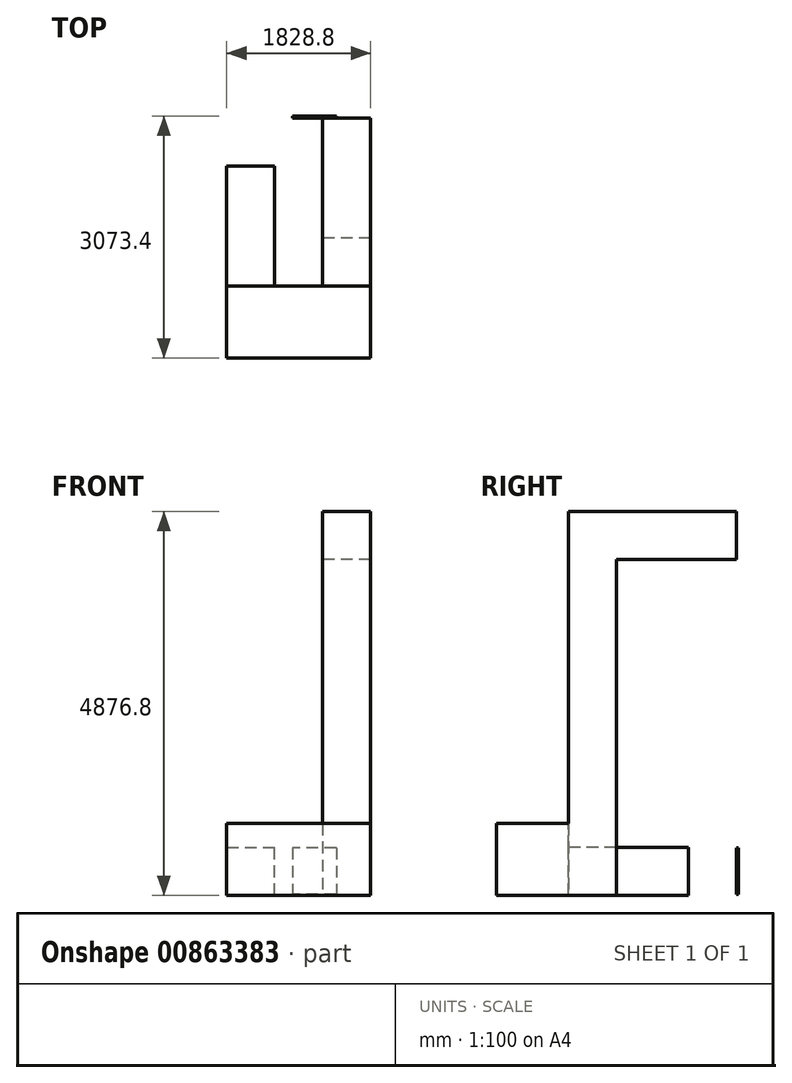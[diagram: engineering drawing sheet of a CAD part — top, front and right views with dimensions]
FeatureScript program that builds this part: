
annotation { "Feature Type Name" : "Feature", "Feature Type Description" : "" }
export const myFeature = defineFeature(function(context is Context, id is Id, definition is map)
    precondition{}
    {
        {
            var Q0;
            Q0=qCreatedBy(makeId("Top.planeOp"),FACE);
            var sketch = newSketch(context, id + "F0", { "sketchPlane" : qUnion([Q0])});
            skLineSegment(sketch, "E0.bottom", {"start": v(0, 0) * mm, "end": v(609.6, 0) * mm});
            skLineSegment(sketch, "E0.top", {"start": v(0, -609.6) * mm, "end": v(609.6, -609.6) * mm});
            skLineSegment(sketch, "E0.left", {"start": v(0, 0) * mm, "end": v(0, -609.6) * mm});
            skLineSegment(sketch, "E0.right", {"start": v(609.6, 0) * mm, "end": v(609.6, -609.6) * mm});
            skSolve(sketch);
        }
        {
            var Q0;
            Q0=makeQuery(id+"F0.imprint","IMPRINT",FACE,{"disambiguationData":[TD([[makeQuery(id+"F0.imprint","IMPRINT",EDGE,{"derivedFrom":sQuery(id+"F0.wireOp",EDGE,"E0.bottom")}),-1.0]])]});
            extrude(context, id + "F1", {"entities" : qUnion([Q0]), "depth" : 4876.8 * mm, "offsetDistance" : 25.4 * mm});
        }
        {
            var Q0;
            Q0=makeQuery(id+"F1.opExtrude","SWEPT_FACE",FACE,{"disambiguationData":[OSD([sQuery(id+"F0.wireOp",EDGE,"E0.bottom")])]});
            var sketch = newSketch(context, id + "F2", { "sketchPlane" : qUnion([Q0])});
            skLineSegment(sketch, "E1.bottom", {"start": v(-609.6, 4876.8) * mm, "end": v(0, 4876.8) * mm});
            skLineSegment(sketch, "E1.top", {"start": v(-609.6, 4267.2) * mm, "end": v(0, 4267.2) * mm});
            skLineSegment(sketch, "E1.left", {"start": v(-609.6, 4876.8) * mm, "end": v(-609.6, 4267.2) * mm});
            skLineSegment(sketch, "E1.right", {"start": v(0, 4876.8) * mm, "end": v(0, 4267.2) * mm});
            skSolve(sketch);
        }
        {
            var Q0;
            Q0=makeQuery(id+"F2.imprint","IMPRINT",FACE,{"disambiguationData":[TD([[makeQuery(id+"F2.imprint","IMPRINT",EDGE,{"derivedFrom":sQuery(id+"F2.wireOp",EDGE,"E1.bottom")}),1.0]])]});
            extrude(context, id + "F3", {"entities" : qUnion([Q0]), "operationType" : NewBodyOperationType.ADD, "depth" : 1524 * mm, "offsetDistance" : 25.4 * mm});
        }
        {
            var Q0;
            Q0=makeQuery(id+"F1.opExtrude","SWEPT_FACE",FACE,{"disambiguationData":[OSD([sQuery(id+"F0.wireOp",EDGE,"E0.top")])]});
            var sketch = newSketch(context, id + "F4", { "sketchPlane" : qUnion([Q0])});
            skLineSegment(sketch, "E2.bottom", {"start": v(609.6, 0) * mm, "end": v(-1219.2, 0) * mm});
            skLineSegment(sketch, "E2.top", {"start": v(609.6, 914.4) * mm, "end": v(-1219.2, 914.4) * mm});
            skLineSegment(sketch, "E2.left", {"start": v(609.6, 0) * mm, "end": v(609.6, 914.4) * mm});
            skLineSegment(sketch, "E2.right", {"start": v(-1219.2, 0) * mm, "end": v(-1219.2, 914.4) * mm});
            skSolve(sketch);
        }
        {
            var Q0;
            {var subQ3=sQuery(id+"F4.wireOp",EDGE,"E2.right");Q0=makeQuery(id+"F4.imprint","IMPRINT",FACE,{"disambiguationData":[TD([[makeQuery(id+"F4.imprint","IMPRINT",EDGE,{"derivedFrom":subQ3}),-1.0]])]});}
            var Q1;
            {var subQ4=sQuery(id+"F4.wireOp",EDGE,"E2.left");Q1=makeQuery(id+"F4.imprint","IMPRINT",FACE,{"disambiguationData":[TD([[makeQuery(id+"F4.imprint","IMPRINT",EDGE,{"derivedFrom":subQ4}),-1.0]])]});}
            extrude(context, id + "F5", {"entities" : qUnion([Q0, Q1]), "operationType" : NewBodyOperationType.ADD, "depth" : 914.4 * mm, "offsetDistance" : 25.4 * mm});
        }
        {
            var Q0;
            Q0=makeQuery(id+"F3.opExtrude","CAP_FACE",FACE,{"disambiguationData":[OSD([sQuery(id+"F2.wireOp",EDGE,"E1.bottom"),sQuery(id+"F2.wireOp",EDGE,"E1.top"),sQuery(id+"F2.wireOp",EDGE,"E1.left"),sQuery(id+"F2.wireOp",EDGE,"E1.right")])],"isStart":false});
            var sketch = newSketch(context, id + "F6", { "sketchPlane" : qUnion([Q0])});
            skLineSegment(sketch, "E3.bottom", {"start": v(-172.87, 606.28) * mm, "end": v(386.94, 606.28) * mm});
            skLineSegment(sketch, "E3.top", {"start": v(-172.87, 11.53) * mm, "end": v(386.94, 11.53) * mm});
            skLineSegment(sketch, "E3.left", {"start": v(-172.87, 606.28) * mm, "end": v(-172.87, 11.53) * mm});
            skLineSegment(sketch, "E3.right", {"start": v(386.94, 606.28) * mm, "end": v(386.94, 11.53) * mm});
            skSolve(sketch);
        }
        {
            var Q0;
            Q0 = qSketchRegion(id + "F6", true);
            extrude(context, id + "F7", {"entities" : qUnion([Q0]), "depth" : 25.4 * mm, "offsetDistance" : 25.4 * mm});
        }
        {
            var Q0;
            Q0=makeQuery(id+"F5.opExtrude","CAP_FACE",FACE,{"disambiguationData":[OSD([sQuery(id+"F4.wireOp",EDGE,"E2.bottom"),sQuery(id+"F4.wireOp",EDGE,"E2.top"),sQuery(id+"F4.wireOp",EDGE,"E2.left"),sQuery(id+"F4.wireOp",EDGE,"E2.right")])],"isStart":true});
            var sketch = newSketch(context, id + "F8", { "sketchPlane" : qUnion([Q0])});
            skLineSegment(sketch, "E4.bottom", {"start": v(1219.2, 0) * mm, "end": v(609.6, 0) * mm});
            skLineSegment(sketch, "E4.top", {"start": v(1219.2, 609.6) * mm, "end": v(609.6, 609.6) * mm});
            skLineSegment(sketch, "E4.left", {"start": v(1219.2, 0) * mm, "end": v(1219.2, 609.6) * mm});
            skLineSegment(sketch, "E4.right", {"start": v(609.6, 0) * mm, "end": v(609.6, 609.6) * mm});
            skSolve(sketch);
        }
        {
            var Q0;
            Q0=makeQuery(id+"F8.imprint","IMPRINT",FACE,{"disambiguationData":[TD([[makeQuery(id+"F8.imprint","IMPRINT",EDGE,{"derivedFrom":sQuery(id+"F8.wireOp",EDGE,"E4.bottom")}),1.0]])]});
            extrude(context, id + "F9", {"entities" : qUnion([Q0]), "operationType" : NewBodyOperationType.ADD, "depth" : 1524 * mm, "offsetDistance" : 25.4 * mm});
        }
    });
